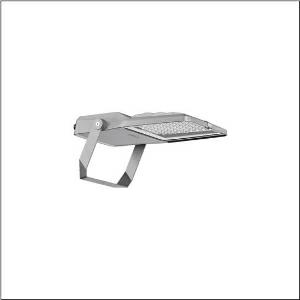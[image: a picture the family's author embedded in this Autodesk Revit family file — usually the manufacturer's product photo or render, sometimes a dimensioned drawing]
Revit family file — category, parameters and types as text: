
# Revit family: floodlight_fl_21_iq_mini___rs12_5xa7771c2b1a_0601
name_source: partatom
category: Lighting Fixtures
units: mm (PartAtom-declared; Revit-internal decimal feet)

## family parameters
Cut with Voids When Loaded = No
Host = Face
Light Source = No
Part Type = Normal
Room Calculation Point = No
Round Connector Dimension = Use Diameter
Shared = No

## types (1)
- --- (1 x LED, 12340 lm, 87.2 W, 3000K)
    Apparent Load = 87 VA
    CIE Flux Codes = 79 92 99 100 100
    Color Rendering = 70
    Color Temperature = 3000K
    Default Elevation = 1800 mm
    Description = Floodlight FL 21 iQ mini, floodlight, primary light control with lens, of PMMA, primary optical cover: protective disc, of toughened safety glass, transparent, light distribution: RS12, light emission: direct distribution, installation type: surface-mounted, LED, High Power LED, rated luminous flux: 12.340lm, luminous efficacy: 142lm/W, light colour: 730, colour temperature: 3000K, control gear: iQ Comfort/DALI, control: Auto-Match, Temp-Guard, Lumen-Switch, Night-Set, Smart-Wire, Light-Fading, Desk-Remote (wireless, voltage-free reading and setting of iQ features in the workshop via application-optimized NFC function/RFID function), optimised constant luminous flux control (CLO 2.0), with terminal, 6-pole, mains connection: 220..240V, AC, 50/60Hz, start of lifetime: 87W, end of service life: 92W, reduction: 40W, luminaire housing, of diecast aluminium, powder-coated, Siteco® metallic grey (DB 702S), corrosivity category C5 mid according to DIN EN ISO 12944, suitable for swimming pools, chlorine-resistant, sealing non-destructively replaceable, mounting bracket, of steel, galvanised, powder-coated, Siteco® metallic grey (DB 702S), protection rating (complete): IP66, insulation class (complete): insulation class II (safety insulation), certification: CE, ENEC, VDE, protection symbol: D, impact resistance: IK08, permissible operating ambient temperature: -40..+40°C, permissible operating ambient temperature for outdoor applications: -40..+50°C, standard: DIN EN 12944, LABS conformity tested according to VDMA 24364:2018-05, packaging unit: 1 piece

Light Distribution: RS12
    Height = 70 mm
    Lamp = 1 x LED
    Lamp Light Flux = 12340 lm
    Lamp Power = 87.2 W
    Lamp count = 1
    Length = 485 mm
    Luminous efficacy = 142 lm/W
    Manufacturer = Siteco
    ModVariant = No
    Model = 5XA7771C2B1A
    Number of Poles = 1
    OnlyDefault = Yes
    Power Factor = 1
    Product Name = Floodlight FL 21 iQ mini | RS12
    Product group = floodlight | pylon annexe
    ProductGroupID = 6200
    Protection Class = Protection class II
    Protection Degree = IP 66
    RLX_Detail_Level = 1
    RLX_Emergency_Light_Flux = 0 lm
    RLX_Emergency_Type = 0
    RLX_Emergency_Type_DB = No
    RlxData = <blob elided: 91353 chars, md5=a553b421>
    Socket = socket
    Standby Power = 0 W
    System Light Flux = 12340 lm
    System Power = 87 W
    Type Comments = factory setting: luminous flux: 100 % | dim-lin: 254 | 456 mA
    Type Image = l_1006845.jpg
    URL = http://relux.com
    VarID = @adj_167744
    Voltage = 0 V
    Weight = 0.00 kg
    Width = 337 mm

## geometry (parser evidence)
native form markers: Blend x4, Sweep x14
no freeform markers — native parametric forms only
